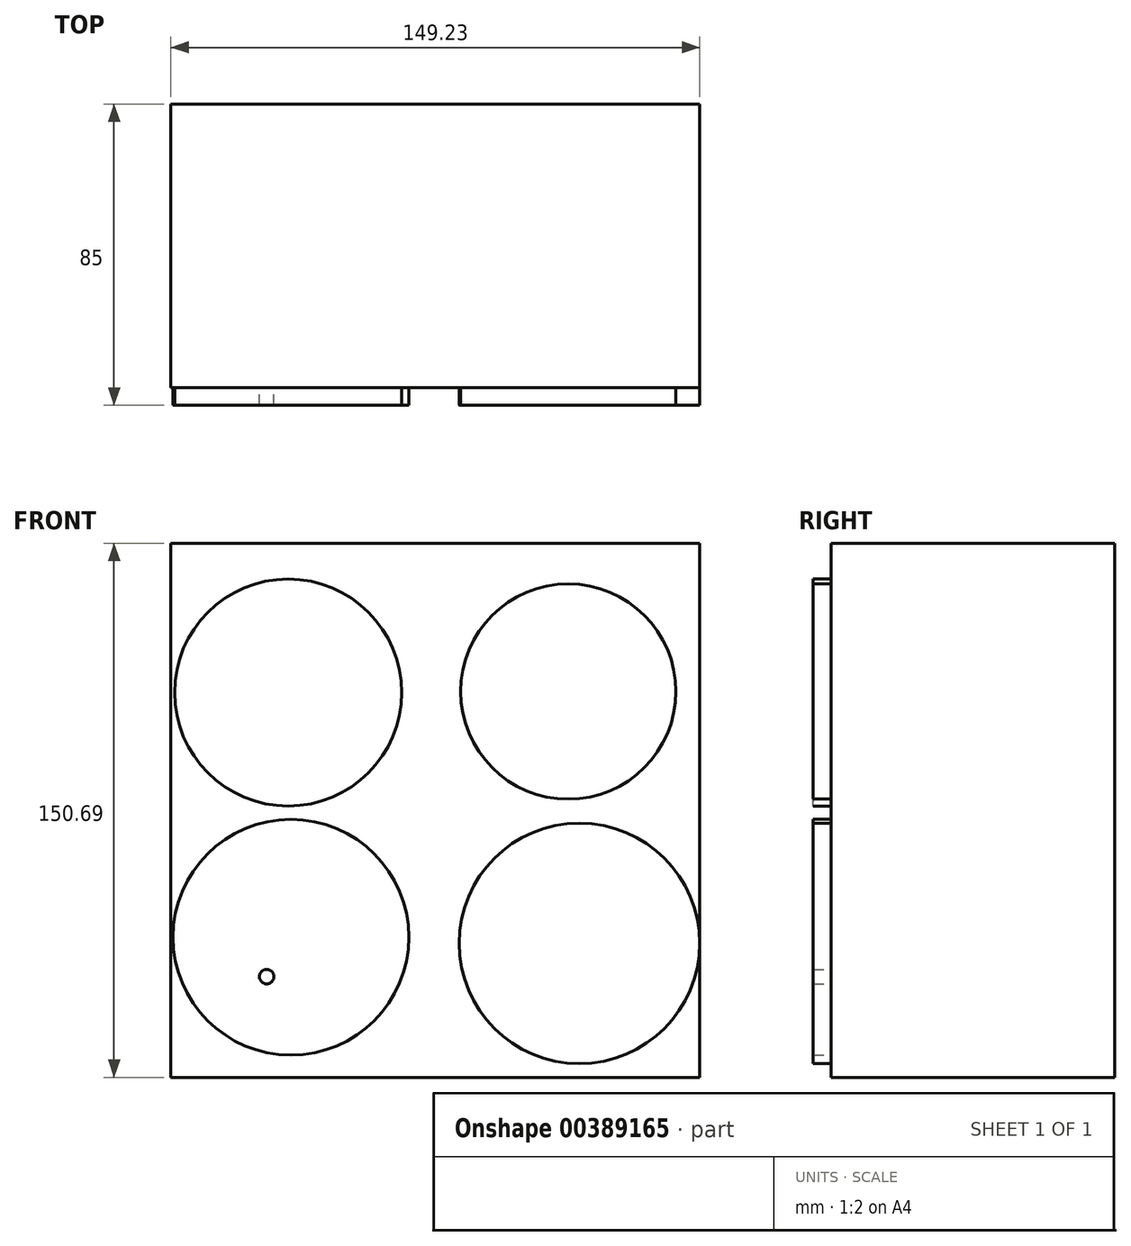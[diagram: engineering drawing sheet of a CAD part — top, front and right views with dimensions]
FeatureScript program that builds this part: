
annotation { "Feature Type Name" : "Feature", "Feature Type Description" : "" }
export const myFeature = defineFeature(function(context is Context, id is Id, definition is map)
    precondition{}
    {
        {
            var Q0;
            Q0=qCreatedBy(makeId("Front.planeOp"),FACE);
            var sketch = newSketch(context, id + "F0", { "sketchPlane" : qUnion([Q0])});
            skLineSegment(sketch, "E0.bottom", {"start": v(-74.9, 75.8) * mm, "end": v(74.32, 75.8) * mm});
            skLineSegment(sketch, "E0.top", {"start": v(-74.9, -74.9) * mm, "end": v(74.32, -74.9) * mm});
            skLineSegment(sketch, "E0.left", {"start": v(-74.9, 75.8) * mm, "end": v(-74.9, -74.9) * mm});
            skLineSegment(sketch, "E0.right", {"start": v(74.32, 75.8) * mm, "end": v(74.32, -74.9) * mm});
            skSolve(sketch);
        }
        {
            var Q0;
            Q0 = qSketchRegion(id + "F0", true);
            extrude(context, id + "F1", {"entities" : qUnion([Q0]), "depth" : 80 * mm});
        }
        {
            var Q0;
            Q0=makeQuery(id+"F1.opExtrude","CAP_FACE",FACE,{"disambiguationData":[OSD([sQuery(id+"F0.wireOp",EDGE,"E0.bottom"),sQuery(id+"F0.wireOp",EDGE,"E0.top"),sQuery(id+"F0.wireOp",EDGE,"E0.left"),sQuery(id+"F0.wireOp",EDGE,"E0.right")])],"isStart":false});
            var sketch = newSketch(context, id + "F2", { "sketchPlane" : qUnion([Q0])});
            skCircle(sketch, "E1", {"center": v(-41.82, 33.7) * mm, "radius": 32.02 * mm});
            skCircle(sketch, "E2", {"center": v(37.2, 34) * mm, "radius": 30.38 * mm});
            skArc(sketch, "E3", {"start": v(-50.18, -32.05) * mm, "mid": v(4.24, -66.1) * mm, "end": v(58.83, -32.34) * mm});
            skSolve(sketch);
        }
        {
            var Q0;
            Q0 = qSketchRegion(id + "F2", true);
            extrude(context, id + "F3", {"entities" : qUnion([Q0]), "operationType" : NewBodyOperationType.ADD, "depth" : 5 * mm});
        }
        {
            var Q0;
            Q0=makeQuery(id+"F1.opExtrude","CAP_FACE",FACE,{"disambiguationData":[OSD([sQuery(id+"F0.wireOp",EDGE,"E0.bottom"),sQuery(id+"F0.wireOp",EDGE,"E0.top"),sQuery(id+"F0.wireOp",EDGE,"E0.left"),sQuery(id+"F0.wireOp",EDGE,"E0.right")])],"isStart":false});
            var sketch = newSketch(context, id + "F4", { "sketchPlane" : qUnion([Q0])});
            skCircle(sketch, "E4", {"center": v(-47.88, -46.47) * mm, "radius": 2.04 * mm});
            skCircle(sketch, "E5", {"center": v(-41.03, -35.36) * mm, "radius": 33.27 * mm});
            skCircle(sketch, "E6", {"center": v(40.34, -37.07) * mm, "radius": 33.93 * mm});
            skSolve(sketch);
        }
        {
            var Q0;
            Q0 = qSketchRegion(id + "F4", true);
            extrude(context, id + "F5", {"entities" : qUnion([Q0]), "operationType" : NewBodyOperationType.ADD, "depth" : 5 * mm});
        }
    });
